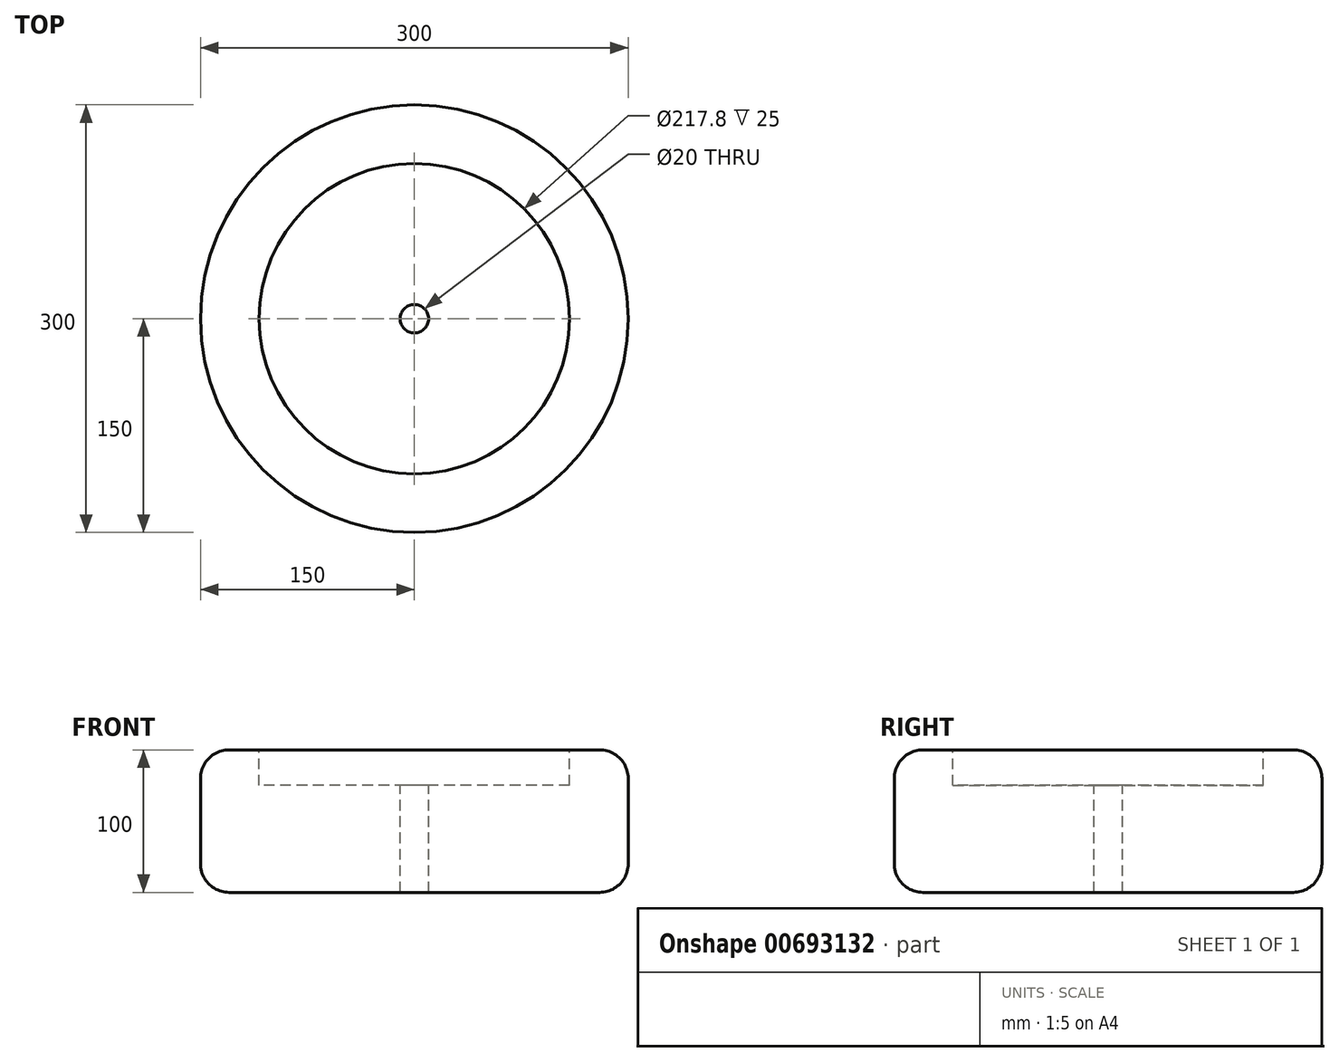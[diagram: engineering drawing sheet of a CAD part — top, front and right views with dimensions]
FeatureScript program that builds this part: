
annotation { "Feature Type Name" : "Feature", "Feature Type Description" : "" }
export const myFeature = defineFeature(function(context is Context, id is Id, definition is map)
    precondition{}
    {
        {
            var Q0;
            Q0=qCreatedBy(makeId("Top.planeOp"),FACE);
            var sketch = newSketch(context, id + "F0", { "sketchPlane" : qUnion([Q0])});
            skCircle(sketch, "E0", {"center": v(0, 0) * mm, "radius": 150 * mm});
            skSolve(sketch);
        }
        {
            var Q0;
            Q0=makeQuery(id+"F0.imprint","IMPRINT",FACE,{"disambiguationData":[TD([[makeQuery(id+"F0.imprint","IMPRINT",EDGE,{"derivedFrom":sQuery(id+"F0.wireOp",EDGE,"E0")}),1.0]])]});
            extrude(context, id + "F1", {"entities" : qUnion([Q0]), "endBound" : BoundingType.SYMMETRIC, "depth" : 100 * mm, "offsetDistance" : 25 * mm});
        }
        {
            var Q0;
            Q0=makeQuery(id+"F1.opExtrude","CAP_EDGE",EDGE,{"disambiguationData":[OSD([sQuery(id+"F0.wireOp",EDGE,"E0")])],"isStart":false});
            var Q1;
            Q1=makeQuery(id+"F1.opExtrude","CAP_EDGE",EDGE,{"disambiguationData":[OSD([sQuery(id+"F0.wireOp",EDGE,"E0")])],"isStart":true});
            fillet(context, id + "F2", {"entities" : qUnion([Q0, Q1]), "radius" : 20 * mm, "tangentPropagation" : true, "allowEdgeOverflow" : false});
        }
        {
            var Q0;
            Q0=makeQuery(id+"F1.opExtrude","CAP_FACE",FACE,{"disambiguationData":[OSD([sQuery(id+"F0.wireOp",EDGE,"E0")])],"isStart":false});
            var sketch = newSketch(context, id + "F3", { "sketchPlane" : qUnion([Q0])});
            skCircle(sketch, "E1", {"center": v(0, 0) * mm, "radius": 108.9 * mm});
            skSolve(sketch);
        }
        {
            var Q0;
            Q0=makeQuery(id+"F3.imprint","IMPRINT",FACE,{"disambiguationData":[TD([[makeQuery(id+"F3.imprint","IMPRINT",EDGE,{"derivedFrom":sQuery(id+"F3.wireOp",EDGE,"E1")}),1.0]])]});
            extrude(context, id + "F4", {"entities" : qUnion([Q0]), "operationType" : NewBodyOperationType.REMOVE, "oppositeDirection" : true, "depth" : 25 * mm, "offsetDistance" : 25 * mm});
        }
        {
            var Q0;
            Q0=makeQuery(id+"F4.boolean.opBoolean","COPY",FACE,{"derivedFrom":makeQuery(id+"F4.opExtrude","CAP_FACE",FACE,{"disambiguationData":[OSD([sQuery(id+"F3.wireOp",EDGE,"E1")])],"isStart":false})});
            var sketch = newSketch(context, id + "F5", { "sketchPlane" : qUnion([Q0])});
            skCircle(sketch, "E2", {"center": v(0, 0) * mm, "radius": 10 * mm});
            skSolve(sketch);
        }
        {
            var Q0;
            Q0=makeQuery(id+"F5.imprint","IMPRINT",FACE,{"disambiguationData":[TD([[makeQuery(id+"F5.imprint","IMPRINT",EDGE,{"derivedFrom":sQuery(id+"F5.wireOp",EDGE,"E2")}),1.0]])]});
            extrude(context, id + "F6", {"entities" : qUnion([Q0]), "operationType" : NewBodyOperationType.REMOVE, "oppositeDirection" : true, "depth" : 150 * mm, "offsetDistance" : 25 * mm});
        }
    });
